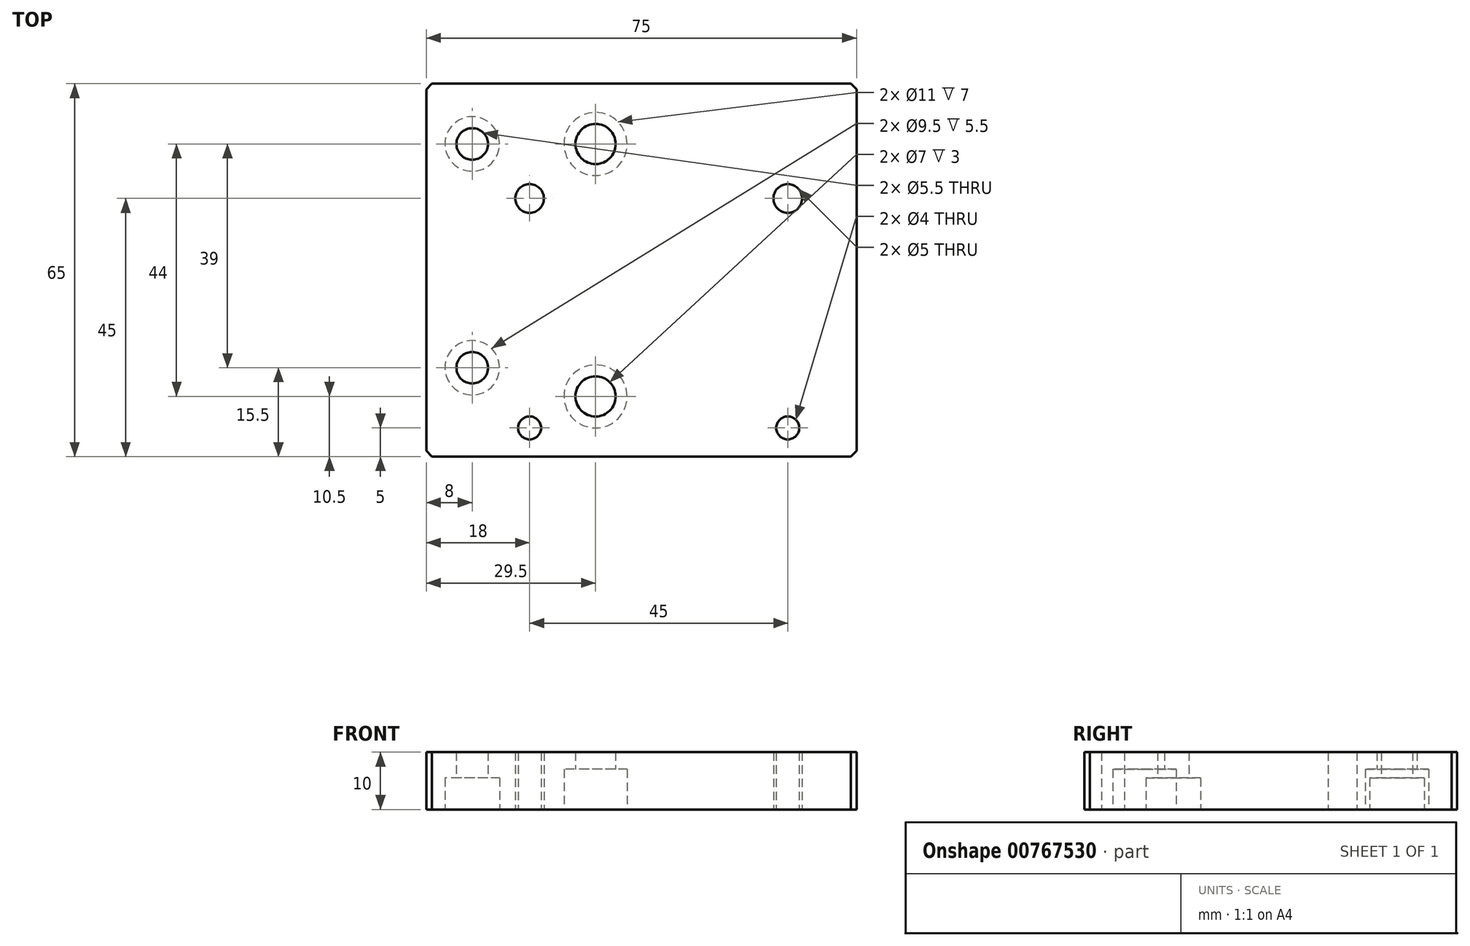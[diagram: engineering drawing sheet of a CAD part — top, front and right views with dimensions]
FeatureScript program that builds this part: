
annotation { "Feature Type Name" : "Feature", "Feature Type Description" : "" }
export const myFeature = defineFeature(function(context is Context, id is Id, definition is map)
    precondition{}
    {
        {
            var Q0;
            Q0=qCreatedBy(makeId("Top.planeOp"),FACE);
            var sketch = newSketch(context, id + "F0", { "sketchPlane" : qUnion([Q0])});
            skLineSegment(sketch, "E0.bottom", {"start": v(-37.5, 32.5) * mm, "end": v(37.5, 32.5) * mm});
            skLineSegment(sketch, "E0.top", {"start": v(-37.5, -32.5) * mm, "end": v(37.5, -32.5) * mm});
            skLineSegment(sketch, "E0.left", {"start": v(-37.5, 32.5) * mm, "end": v(-37.5, -32.5) * mm});
            skLineSegment(sketch, "E0.right", {"start": v(37.5, 32.5) * mm, "end": v(37.5, -32.5) * mm});
            skPoint(sketch, "E0.middle", {"position": v(0, 0) * mm});
            skSolve(sketch);
        }
        {
            var Q0;
            Q0 = qSketchRegion(id + "F0", true);
            var sketch = newSketch(context, id + "F1", { "sketchPlane" : qUnion([Q0])});
            skSolve(sketch);
        }
        {
            var Q0;
            Q0=makeQuery(id+"F1.imprint","IMPRINT",FACE,{"disambiguationData":[TD([[makeQuery(id+"F1.imprint","IMPRINT",EDGE,{"derivedFrom":makeQuery(id+"F0.imprint","IMPRINT",EDGE,{"derivedFrom":sQuery(id+"F0.wireOp",EDGE,"E0.bottom")})}),-1.0]])]});
            extrude(context, id + "F2", {"entities" : qUnion([Q0]), "depth" : 10 * mm, "offsetDistance" : 25 * mm});
        }
        {
            var Q0;
            Q0 = qSketchRegion(id + "F0", true);
            var sketch = newSketch(context, id + "F3", { "sketchPlane" : qUnion([Q0])});
            skCircle(sketch, "E1", {"center": v(-29.5, -17) * mm, "radius": 4.75 * mm, "construction": true});
            skCircle(sketch, "E2", {"center": v(-29.5, 22) * mm, "radius": 4.75 * mm, "construction": true});
            skCircle(sketch, "E3", {"center": v(-8, 22) * mm, "radius": 5.5 * mm});
            skCircle(sketch, "E4", {"center": v(-8, -22) * mm, "radius": 5.5 * mm});
            skSolve(sketch);
        }
        {
            var Q0;
            Q0 = qSketchRegion(id + "F3", true);
            extrude(context, id + "F4", {"entities" : qUnion([Q0]), "operationType" : NewBodyOperationType.REMOVE, "depth" : 7 * mm, "offsetDistance" : 25 * mm});
        }
        {
            var Q0;
            Q0 = qSketchRegion(id + "F0", true);
            var sketch = newSketch(context, id + "F5", { "sketchPlane" : qUnion([Q0])});
            skCircle(sketch, "E5", {"center": v(-29.5, 22) * mm, "radius": 4.75 * mm});
            skCircle(sketch, "E6", {"center": v(-29.5, -17) * mm, "radius": 4.75 * mm});
            skSolve(sketch);
        }
        {
            var Q0;
            Q0 = qSketchRegion(id + "F5", true);
            extrude(context, id + "F6", {"entities" : qUnion([Q0]), "operationType" : NewBodyOperationType.REMOVE, "depth" : 5.5 * mm, "offsetDistance" : 25 * mm});
        }
        {
            var Q0;
            Q0=makeQuery(id+"F0.imprint","IMPRINT",FACE,{"disambiguationData":[TD([[makeQuery(id+"F0.imprint","IMPRINT",EDGE,{"derivedFrom":sQuery(id+"F0.wireOp",EDGE,"E0.bottom")}),-1.0]])]});
            var sketch = newSketch(context, id + "F7", { "sketchPlane" : qUnion([Q0])});
            skCircle(sketch, "E7", {"center": v(-8, -22) * mm, "radius": 3.5 * mm});
            skCircle(sketch, "E8", {"center": v(-8, 22) * mm, "radius": 3.5 * mm});
            skSolve(sketch);
        }
        {
            var Q0;
            Q0 = qSketchRegion(id + "F7", true);
            extrude(context, id + "F8", {"entities" : qUnion([Q0]), "operationType" : NewBodyOperationType.REMOVE, "depth" : 25 * mm, "offsetDistance" : 25 * mm});
        }
        {
            var Q0;
            Q0=makeQuery(id+"F0.imprint","IMPRINT",FACE,{"disambiguationData":[TD([[makeQuery(id+"F0.imprint","IMPRINT",EDGE,{"derivedFrom":sQuery(id+"F0.wireOp",EDGE,"E0.bottom")}),-1.0]])]});
            var sketch = newSketch(context, id + "F9", { "sketchPlane" : qUnion([Q0])});
            skCircle(sketch, "E9", {"center": v(-29.5, -17) * mm, "radius": 2.75 * mm});
            skCircle(sketch, "E10", {"center": v(-29.5, 22) * mm, "radius": 2.75 * mm});
            skSolve(sketch);
        }
        {
            var Q0;
            Q0 = qSketchRegion(id + "F9", true);
            extrude(context, id + "F10", {"entities" : qUnion([Q0]), "operationType" : NewBodyOperationType.REMOVE, "depth" : 25 * mm, "offsetDistance" : 25 * mm});
        }
        {
            var Q0;
            Q0=makeQuery(id+"F0.imprint","IMPRINT",FACE,{"disambiguationData":[TD([[makeQuery(id+"F0.imprint","IMPRINT",EDGE,{"derivedFrom":sQuery(id+"F0.wireOp",EDGE,"E0.bottom")}),-1.0]])]});
            var sketch = newSketch(context, id + "F11", { "sketchPlane" : qUnion([Q0])});
            skCircle(sketch, "E11", {"center": v(-19.5, -27.5) * mm, "radius": 2 * mm});
            skCircle(sketch, "E12", {"center": v(-19.5, 12.5) * mm, "radius": 2.5 * mm});
            skCircle(sketch, "E13", {"center": v(25.5, -27.5) * mm, "radius": 2 * mm});
            skCircle(sketch, "E14", {"center": v(25.5, 12.5) * mm, "radius": 2.5 * mm});
            skSolve(sketch);
        }
        {
            var Q0;
            Q0 = qSketchRegion(id + "F11", true);
            extrude(context, id + "F12", {"entities" : qUnion([Q0]), "operationType" : NewBodyOperationType.REMOVE, "depth" : 25 * mm, "offsetDistance" : 25 * mm});
        }
        {
            var Q0;
            Q0=makeQuery(id+"F2.opExtrude","SWEPT_EDGE",EDGE,{"disambiguationData":[OSD([sQuery(id+"F0.wireOp",EDGE,"E0.bottom"),sQuery(id+"F0.wireOp",EDGE,"E0.left")])]});
            var Q1;
            Q1=makeQuery(id+"F2.opExtrude","SWEPT_EDGE",EDGE,{"disambiguationData":[OSD([sQuery(id+"F0.wireOp",EDGE,"E0.top"),sQuery(id+"F0.wireOp",EDGE,"E0.left")])]});
            var Q2;
            Q2=makeQuery(id+"F2.opExtrude","SWEPT_EDGE",EDGE,{"disambiguationData":[OSD([sQuery(id+"F0.wireOp",EDGE,"E0.top"),sQuery(id+"F0.wireOp",EDGE,"E0.right")])]});
            var Q3;
            Q3=makeQuery(id+"F2.opExtrude","SWEPT_EDGE",EDGE,{"disambiguationData":[OSD([sQuery(id+"F0.wireOp",EDGE,"E0.bottom"),sQuery(id+"F0.wireOp",EDGE,"E0.right")])]});
            chamfer(context, id + "F13", {"entities" : qUnion([Q0, Q1, Q2, Q3]), "width" : 1 * mm, "tangentPropagation" : true});
        }
    });
